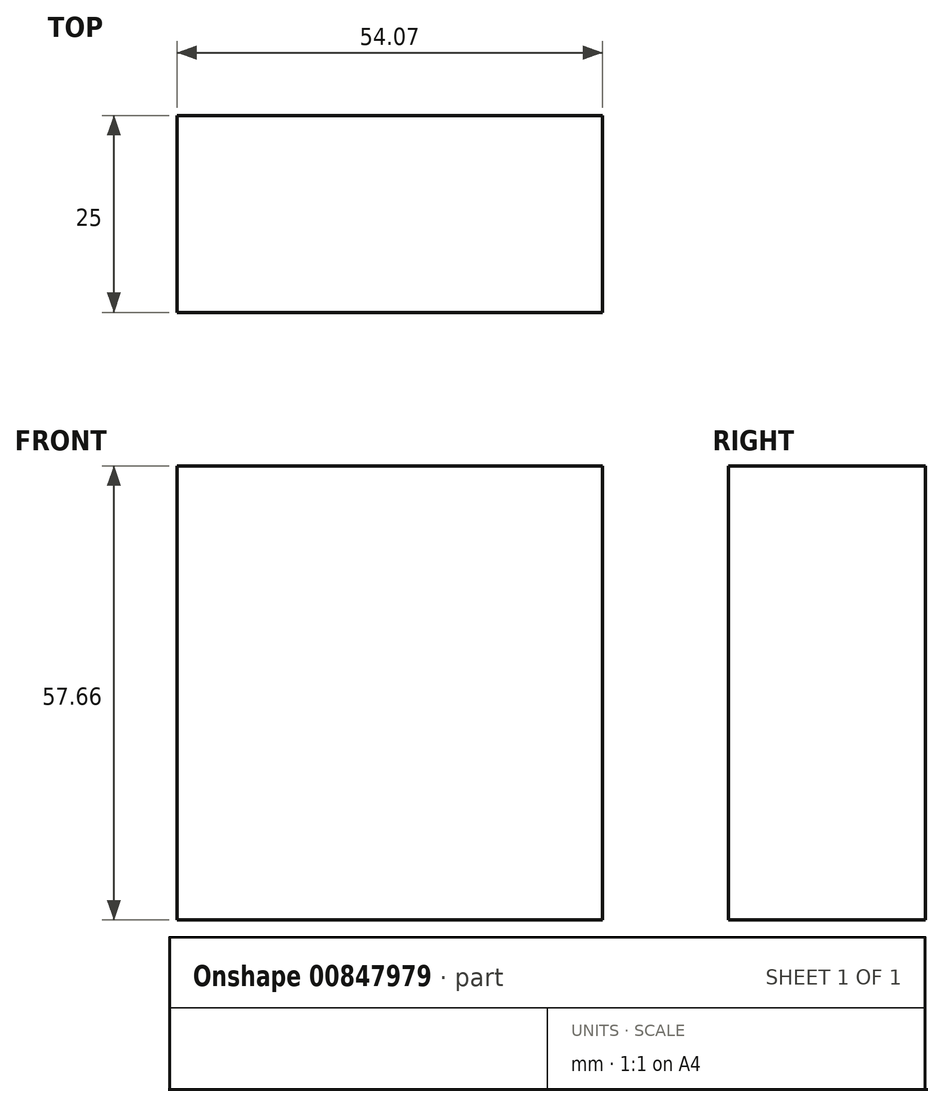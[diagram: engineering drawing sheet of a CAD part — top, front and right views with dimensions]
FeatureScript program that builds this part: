
annotation { "Feature Type Name" : "Feature", "Feature Type Description" : "" }
export const myFeature = defineFeature(function(context is Context, id is Id, definition is map)
    precondition{}
    {
        {
            var Q0;
            Q0=qCreatedBy(makeId("Front.planeOp"),FACE);
            var sketch = newSketch(context, id + "F0", { "sketchPlane" : qUnion([Q0])});
            skLineSegment(sketch, "E0.bottom", {"start": v(-140.2, 9.1) * mm, "end": v(-86.12, 9.1) * mm});
            skLineSegment(sketch, "E0.top", {"start": v(-140.2, 66.76) * mm, "end": v(-86.12, 66.76) * mm});
            skLineSegment(sketch, "E0.left", {"start": v(-140.2, 9.1) * mm, "end": v(-140.2, 66.76) * mm});
            skLineSegment(sketch, "E0.right", {"start": v(-86.12, 9.1) * mm, "end": v(-86.12, 66.76) * mm});
            skPoint(sketch, "E0.middle", {"position": v(-113.15, 37.93) * mm});
            skSolve(sketch);
        }
        {
            var Q0;
            Q0=makeQuery(id+"F0.imprint","IMPRINT",FACE,{"disambiguationData":[TD([[makeQuery(id+"F0.imprint","IMPRINT",EDGE,{"derivedFrom":sQuery(id+"F0.wireOp",EDGE,"E0.bottom")}),1.0]])]});
            extrude(context, id + "F1", {"entities" : qUnion([Q0]), "depth" : 25 * mm, "offsetDistance" : 25 * mm});
        }
    });
